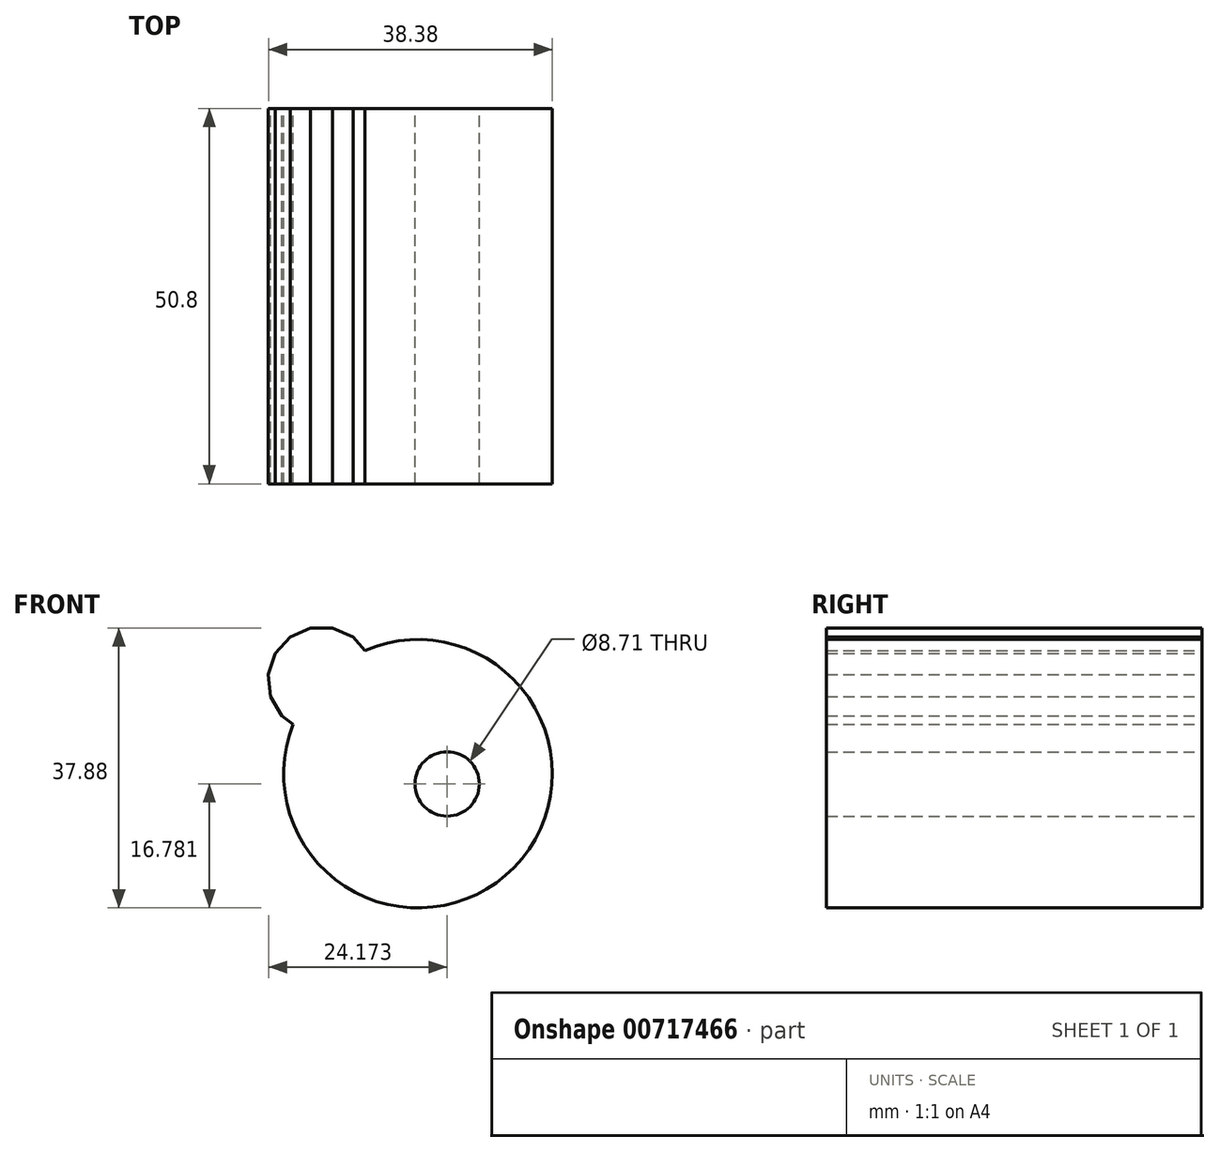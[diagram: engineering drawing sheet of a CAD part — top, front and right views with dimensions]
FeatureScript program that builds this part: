
annotation { "Feature Type Name" : "Feature", "Feature Type Description" : "" }
export const myFeature = defineFeature(function(context is Context, id is Id, definition is map)
    precondition{}
    {
        {
            var Q0;
            Q0=qCreatedBy(makeId("Front.planeOp"),FACE);
            var sketch = newSketch(context, id + "F0", { "sketchPlane" : qUnion([Q0])});
            skCircle(sketch, "E0", {"center": v(-33.92, 38.18) * mm, "radius": 18.16 * mm});
            skCircle(sketch, "E1.cCircle", {"center": v(-46.96, 50.82) * mm, "radius": 7.07 * mm, "construction": true});
            skLineSegment(sketch, "E1.0", {"start": v(-40.1, 48.57) * mm, "end": v(-41.6, 45.97) * mm});
            skLineSegment(sketch, "E1.1", {"start": v(-41.6, 45.97) * mm, "end": v(-44.03, 44.21) * mm});
            skLineSegment(sketch, "E1.2", {"start": v(-44.03, 44.21) * mm, "end": v(-46.97, 43.6) * mm});
            skLineSegment(sketch, "E1.3", {"start": v(-46.97, 43.6) * mm, "end": v(-49.91, 44.22) * mm});
            skLineSegment(sketch, "E1.4", {"start": v(-49.91, 44.22) * mm, "end": v(-52.34, 46) * mm});
            skLineSegment(sketch, "E1.5", {"start": v(-52.34, 46) * mm, "end": v(-53.84, 48.6) * mm});
            skLineSegment(sketch, "E1.6", {"start": v(-53.84, 48.6) * mm, "end": v(-54.14, 51.59) * mm});
            skLineSegment(sketch, "E1.7", {"start": v(-54.14, 51.59) * mm, "end": v(-53.21, 54.44) * mm});
            skLineSegment(sketch, "E1.8", {"start": v(-53.21, 54.44) * mm, "end": v(-51.2, 56.67) * mm});
            skLineSegment(sketch, "E1.9", {"start": v(-51.2, 56.67) * mm, "end": v(-48.45, 57.89) * mm});
            skLineSegment(sketch, "E1.10", {"start": v(-48.45, 57.89) * mm, "end": v(-45.45, 57.88) * mm});
            skLineSegment(sketch, "E1.11", {"start": v(-45.45, 57.88) * mm, "end": v(-42.7, 56.66) * mm});
            skLineSegment(sketch, "E1.12", {"start": v(-42.7, 56.66) * mm, "end": v(-40.7, 54.42) * mm});
            skLineSegment(sketch, "E1.13", {"start": v(-40.7, 54.42) * mm, "end": v(-39.77, 51.56) * mm});
            skLineSegment(sketch, "E1.14", {"start": v(-39.77, 51.56) * mm, "end": v(-40.1, 48.57) * mm});
            skPoint(sketch, "E1.0.midPoint", {"position": v(-40.85, 47.27) * mm});
            skCircle(sketch, "E2", {"center": v(-29.97, 36.8) * mm, "radius": 4.36 * mm});
            skPoint(sketch, "E3", {"position": v(-42.82, 33.82) * mm});
            skSolve(sketch);
        }
        {
            var Q0;
            Q0 = qSketchRegion(id + "F0", true);
            var Q1;
            Q1=makeQuery(id+"F0.imprint","IMPRINT",FACE,{"disambiguationData":[TD([[makeQuery(id+"F0.imprint","IMPRINT",EDGE,{"derivedFrom":sQuery(id+"F0.wireOp",EDGE,"E1.0")}),1.0]])]});
            extrude(context, id + "F1", {"entities" : qUnion([Q0, Q1]), "depth" : 50.8 * mm, "offsetDistance" : 25.4 * mm});
        }
    });
